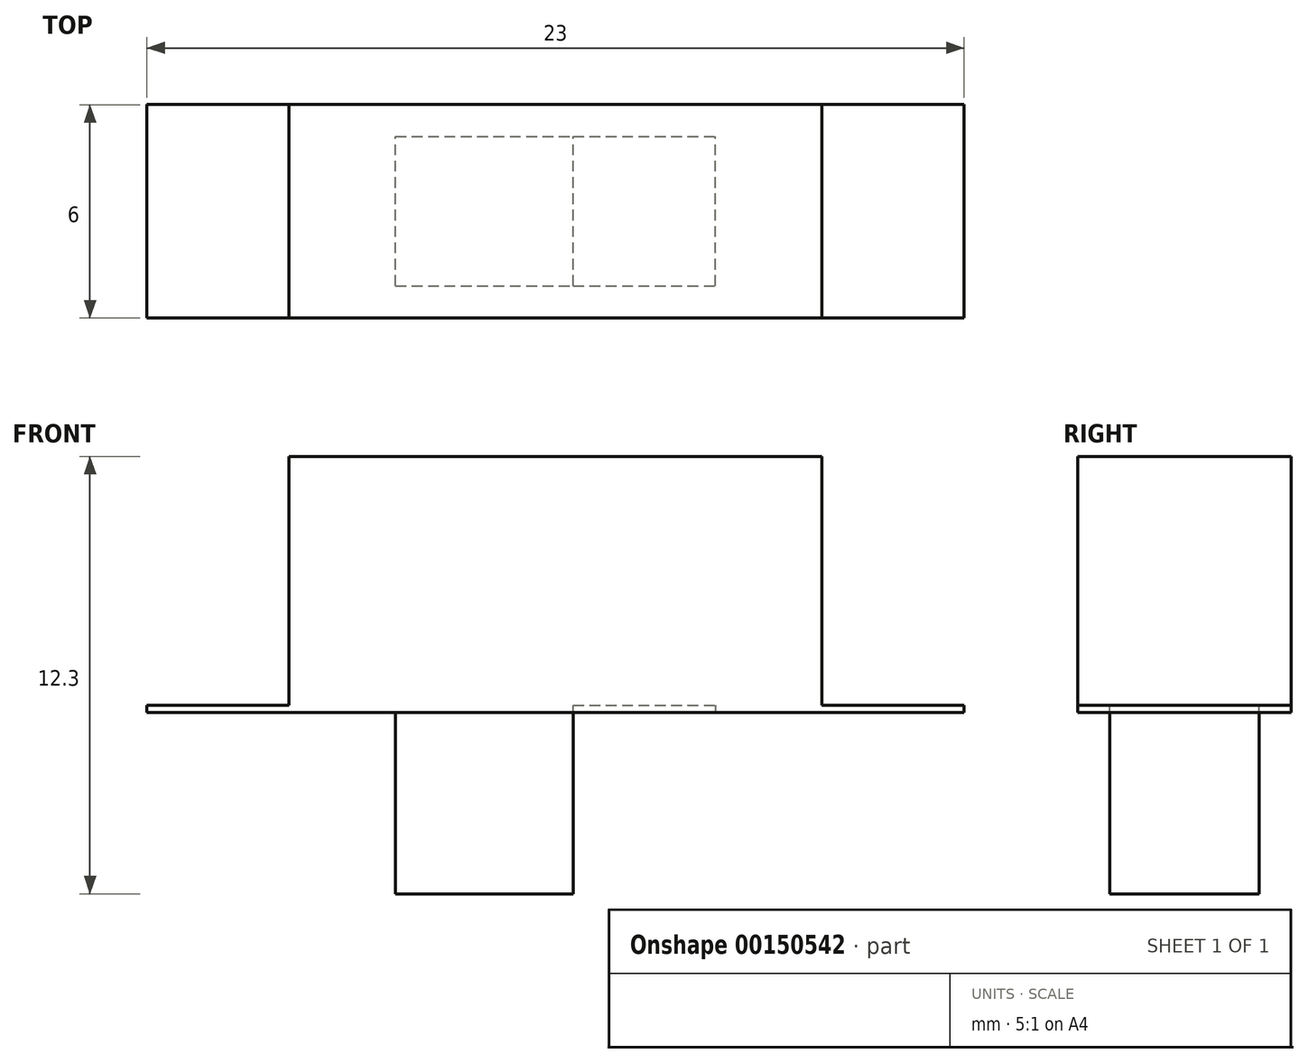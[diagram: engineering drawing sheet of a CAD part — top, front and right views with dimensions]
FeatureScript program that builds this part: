
annotation { "Feature Type Name" : "Feature", "Feature Type Description" : "" }
export const myFeature = defineFeature(function(context is Context, id is Id, definition is map)
    precondition{}
    {
        {
            var Q0;
            Q0=qCreatedBy(makeId("Top.planeOp"),FACE);
            var sketch = newSketch(context, id + "F0", { "sketchPlane" : qUnion([Q0])});
            skLineSegment(sketch, "E0.bottom", {"start": v(-29.96, -5.36) * mm, "end": v(-6.96, -5.36) * mm});
            skLineSegment(sketch, "E0.top", {"start": v(-29.96, -11.36) * mm, "end": v(-6.96, -11.36) * mm});
            skLineSegment(sketch, "E0.left", {"start": v(-29.96, -5.36) * mm, "end": v(-29.96, -11.36) * mm});
            skLineSegment(sketch, "E0.right", {"start": v(-6.96, -5.36) * mm, "end": v(-6.96, -11.36) * mm});
            skSolve(sketch);
        }
        {
            var Q0;
            Q0=makeQuery(id+"F0.imprint","IMPRINT",FACE,{"disambiguationData":[TD([[makeQuery(id+"F0.imprint","IMPRINT",EDGE,{"derivedFrom":sQuery(id+"F0.wireOp",EDGE,"E0.bottom")}),-1.0]])]});
            extrude(context, id + "F1", {"entities" : qUnion([Q0]), "depth" : 0.2 * mm});
        }
        {
            var Q0;
            Q0=makeQuery(id+"F1.opExtrude","CAP_FACE",FACE,{"disambiguationData":[OSD([sQuery(id+"F0.wireOp",EDGE,"E0.bottom"),sQuery(id+"F0.wireOp",EDGE,"E0.top"),sQuery(id+"F0.wireOp",EDGE,"E0.left"),sQuery(id+"F0.wireOp",EDGE,"E0.right")])],"isStart":false});
            var sketch = newSketch(context, id + "F2", { "sketchPlane" : qUnion([Q0])});
            skLineSegment(sketch, "E1.bottom", {"start": v(-25.96, -11.36) * mm, "end": v(-10.96, -11.36) * mm});
            skLineSegment(sketch, "E1.top", {"start": v(-25.96, -5.36) * mm, "end": v(-10.96, -5.36) * mm});
            skLineSegment(sketch, "E1.left", {"start": v(-25.96, -11.36) * mm, "end": v(-25.96, -5.36) * mm});
            skLineSegment(sketch, "E1.right", {"start": v(-10.96, -11.36) * mm, "end": v(-10.96, -5.36) * mm});
            skSolve(sketch);
        }
        {
            var Q0;
            Q0=makeQuery(id+"F2.imprint","IMPRINT",FACE,{"disambiguationData":[TD([[makeQuery(id+"F2.imprint","IMPRINT",EDGE,{"derivedFrom":sQuery(id+"F2.wireOp",EDGE,"E1.bottom")}),1.0]])]});
            extrude(context, id + "F3", {"entities" : qUnion([Q0]), "operationType" : NewBodyOperationType.ADD, "depth" : 7 * mm});
        }
        {
            var Q0;
            Q0=makeQuery(id+"F1.opExtrude","CAP_FACE",FACE,{"disambiguationData":[OSD([sQuery(id+"F0.wireOp",EDGE,"E0.bottom"),sQuery(id+"F0.wireOp",EDGE,"E0.top"),sQuery(id+"F0.wireOp",EDGE,"E0.left"),sQuery(id+"F0.wireOp",EDGE,"E0.right")])],"isStart":true});
            var sketch = newSketch(context, id + "F4", { "sketchPlane" : qUnion([Q0])});
            skLineSegment(sketch, "E2.bottom", {"start": v(-22.96, 10.46) * mm, "end": v(-13.96, 10.46) * mm});
            skLineSegment(sketch, "E2.top", {"start": v(-22.96, 6.26) * mm, "end": v(-13.96, 6.26) * mm});
            skLineSegment(sketch, "E2.left", {"start": v(-22.96, 10.46) * mm, "end": v(-22.96, 6.26) * mm});
            skLineSegment(sketch, "E2.right", {"start": v(-13.96, 10.46) * mm, "end": v(-13.96, 6.26) * mm});
            skLineSegment(sketch, "E3", {"start": v(-29.96, 8.36) * mm, "end": v(-6.96, 8.36) * mm, "construction": true});
            skLineSegment(sketch, "E4", {"start": v(-18.46, 11.36) * mm, "end": v(-18.46, 5.36) * mm, "construction": true});
            skLineSegment(sketch, "E5", {"start": v(-18.46, 10.46) * mm, "end": v(-18.46, 6.26) * mm, "construction": true});
            skLineSegment(sketch, "E6", {"start": v(-22.96, 8.36) * mm, "end": v(-13.96, 8.36) * mm, "construction": true});
            skSolve(sketch);
        }
        {
            var Q0;
            Q0=makeQuery(id+"F4.imprint","IMPRINT",FACE,{"disambiguationData":[TD([[makeQuery(id+"F4.imprint","IMPRINT",EDGE,{"derivedFrom":sQuery(id+"F4.wireOp",EDGE,"E2.bottom")}),-1.0]])]});
            extrude(context, id + "F5", {"entities" : qUnion([Q0]), "operationType" : NewBodyOperationType.REMOVE, "oppositeDirection" : true, "depth" : 0.2 * mm});
        }
        {
            var Q0;
            Q0=makeQuery(id+"F5.boolean.opBoolean","COPY",FACE,{"derivedFrom":makeQuery(id+"F5.opExtrude","CAP_FACE",FACE,{"disambiguationData":[OSD([sQuery(id+"F4.wireOp",EDGE,"E2.bottom"),sQuery(id+"F4.wireOp",EDGE,"E2.top"),sQuery(id+"F4.wireOp",EDGE,"E2.left"),sQuery(id+"F4.wireOp",EDGE,"E2.right")])],"isStart":false})});
            var sketch = newSketch(context, id + "F6", { "sketchPlane" : qUnion([Q0])});
            skLineSegment(sketch, "E7.bottom", {"start": v(-22.96, 10.46) * mm, "end": v(-17.96, 10.46) * mm});
            skLineSegment(sketch, "E7.top", {"start": v(-22.96, 6.26) * mm, "end": v(-17.96, 6.26) * mm});
            skLineSegment(sketch, "E7.left", {"start": v(-22.96, 10.46) * mm, "end": v(-22.96, 6.26) * mm});
            skLineSegment(sketch, "E7.right", {"start": v(-17.96, 10.46) * mm, "end": v(-17.96, 6.26) * mm});
            skSolve(sketch);
        }
        {
            var Q0;
            Q0 = qSketchRegion(id + "F6", true);
            var Q1;
            Q1=makeQuery(id+"F6.imprint","IMPRINT",FACE,{"disambiguationData":[TD([[makeQuery(id+"F6.imprint","IMPRINT",EDGE,{"derivedFrom":sQuery(id+"F6.wireOp",EDGE,"E7.bottom")}),-1.0]])]});
            extrude(context, id + "F7", {"entities" : qUnion([Q0, Q1]), "operationType" : NewBodyOperationType.ADD, "depth" : 5.3 * mm});
        }
    });
